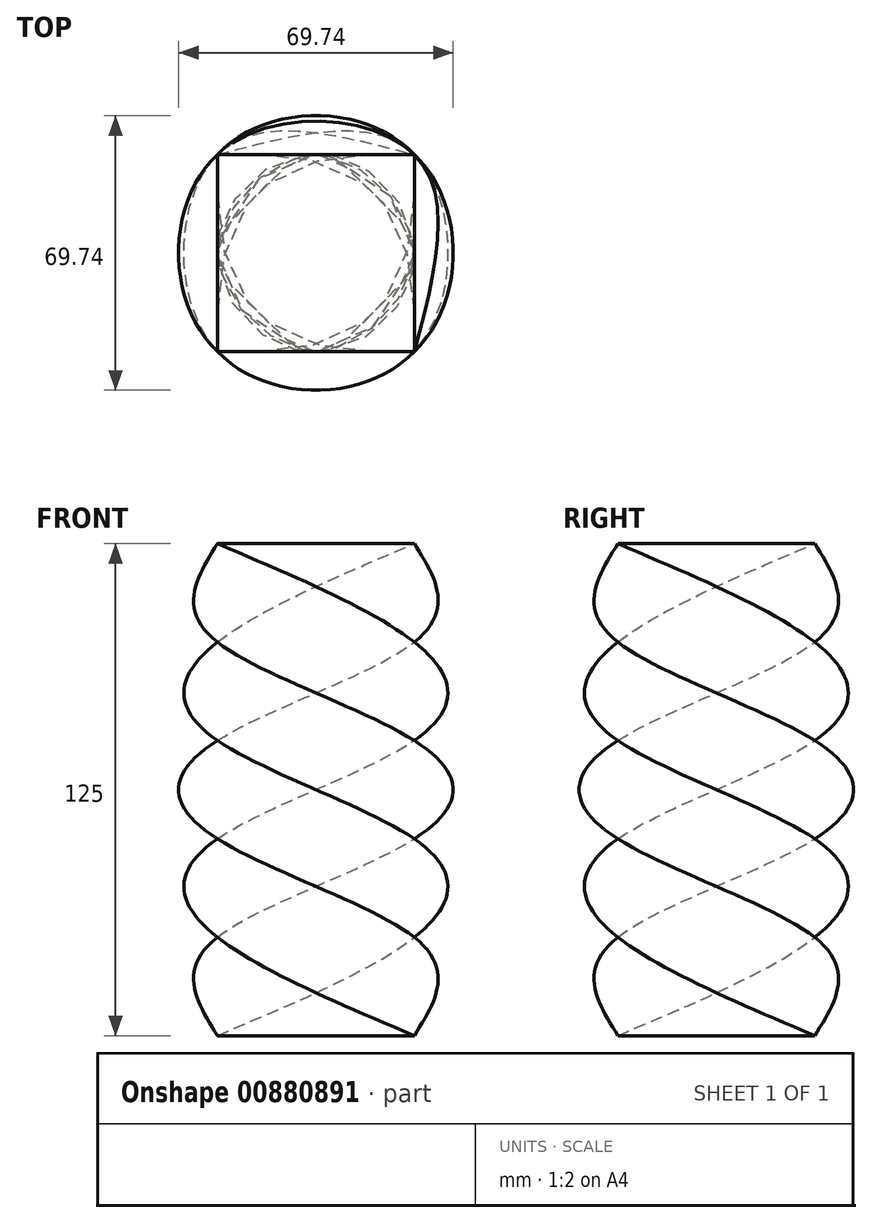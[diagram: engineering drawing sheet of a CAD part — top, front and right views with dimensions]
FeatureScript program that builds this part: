
annotation { "Feature Type Name" : "Feature", "Feature Type Description" : "" }
export const myFeature = defineFeature(function(context is Context, id is Id, definition is map)
    precondition{}
    {
        {
            var Q0;
            Q0=qCreatedBy(makeId("Top.planeOp"),FACE);
            cPlane(context, id + "F0", {"entities" : qUnion([Q0]), "cplaneType" : CPlaneType.OFFSET, "offset" : 25 * mm, "width" : 150 * mm, "height" : 150 * mm});
        }
        {
            var Q0;
            Q0=qCreatedBy(id+"F0.planeOp",FACE);
            cPlane(context, id + "F1", {"entities" : qUnion([Q0]), "cplaneType" : CPlaneType.OFFSET, "offset" : 25 * mm, "width" : 150 * mm, "height" : 150 * mm});
        }
        {
            var Q0;
            Q0=qCreatedBy(id+"F1.planeOp",FACE);
            cPlane(context, id + "F2", {"entities" : qUnion([Q0]), "cplaneType" : CPlaneType.OFFSET, "offset" : 25 * mm, "width" : 150 * mm, "height" : 150 * mm});
        }
        {
            var Q0;
            Q0=qCreatedBy(id+"F2.planeOp",FACE);
            cPlane(context, id + "F3", {"entities" : qUnion([Q0]), "cplaneType" : CPlaneType.OFFSET, "offset" : 25 * mm, "width" : 150 * mm, "height" : 150 * mm});
        }
        {
            var Q0;
            Q0=qCreatedBy(id+"F3.planeOp",FACE);
            cPlane(context, id + "F4", {"entities" : qUnion([Q0]), "cplaneType" : CPlaneType.OFFSET, "offset" : 25 * mm, "width" : 150 * mm, "height" : 150 * mm});
        }
        {
            var Q0;
            Q0=qCreatedBy(makeId("Top.planeOp"),FACE);
            var sketch = newSketch(context, id + "F5", { "sketchPlane" : qUnion([Q0])});
            skLineSegment(sketch, "E0.bottom", {"start": v(25, 25) * mm, "end": v(-25, 25) * mm});
            skLineSegment(sketch, "E0.top", {"start": v(25, -25) * mm, "end": v(-25, -25) * mm});
            skLineSegment(sketch, "E0.left", {"start": v(25, 25) * mm, "end": v(25, -25) * mm});
            skLineSegment(sketch, "E0.right", {"start": v(-25, 25) * mm, "end": v(-25, -25) * mm});
            skPoint(sketch, "E0.middle", {"position": v(0, 0) * mm});
            skSolve(sketch);
        }
        {
            var Q0;
            Q0=qCreatedBy(id+"F0.planeOp",FACE);
            var sketch = newSketch(context, id + "F6", { "sketchPlane" : qUnion([Q0])});
            skLineSegment(sketch, "E1.0", {"start": v(25, -25) * mm, "end": v(-25, -25) * mm});
            skLineSegment(sketch, "E2.0", {"start": v(25, 25) * mm, "end": v(25, -25) * mm});
            skLineSegment(sketch, "E3.0", {"start": v(-25, 25) * mm, "end": v(-25, -25) * mm});
            skLineSegment(sketch, "E4.0", {"start": v(25, 25) * mm, "end": v(-25, 25) * mm});
            skPoint(sketch, "E5.0", {"position": v(0, 0) * mm});
            skSolve(sketch);
        }
        {
            var Q0;
            Q0=qCreatedBy(id+"F1.planeOp",FACE);
            var sketch = newSketch(context, id + "F7", { "sketchPlane" : qUnion([Q0])});
            skPoint(sketch, "E6.0", {"position": v(0, 0) * mm});
            skLineSegment(sketch, "E7.0", {"start": v(-25, 25) * mm, "end": v(-25, -25) * mm});
            skLineSegment(sketch, "E8.0", {"start": v(25, 25) * mm, "end": v(25, -25) * mm});
            skLineSegment(sketch, "E9.0", {"start": v(25, -25) * mm, "end": v(-25, -25) * mm});
            skLineSegment(sketch, "E10.0", {"start": v(25, 25) * mm, "end": v(-25, 25) * mm});
            skSolve(sketch);
        }
        {
            var Q0;
            Q0=qCreatedBy(id+"F2.planeOp",FACE);
            var sketch = newSketch(context, id + "F8", { "sketchPlane" : qUnion([Q0])});
            skLineSegment(sketch, "E11.0", {"start": v(25, 25) * mm, "end": v(-25, 25) * mm});
            skLineSegment(sketch, "E12.0", {"start": v(-25, 25) * mm, "end": v(-25, -25) * mm});
            skLineSegment(sketch, "E13.0", {"start": v(25, 25) * mm, "end": v(25, -25) * mm});
            skPoint(sketch, "E14.0", {"position": v(0, 0) * mm});
            skLineSegment(sketch, "E15.0", {"start": v(25, -25) * mm, "end": v(-25, -25) * mm});
            skSolve(sketch);
        }
        {
            var Q0;
            Q0=qCreatedBy(id+"F3.planeOp",FACE);
            var sketch = newSketch(context, id + "F9", { "sketchPlane" : qUnion([Q0])});
            skLineSegment(sketch, "E16.0", {"start": v(25, 25) * mm, "end": v(-25, 25) * mm});
            skLineSegment(sketch, "E17.0", {"start": v(-25, 25) * mm, "end": v(-25, -25) * mm});
            skLineSegment(sketch, "E18.0", {"start": v(25, 25) * mm, "end": v(25, -25) * mm});
            skLineSegment(sketch, "E19.0", {"start": v(25, -25) * mm, "end": v(-25, -25) * mm});
            skPoint(sketch, "E20.0", {"position": v(0, 0) * mm});
            skSolve(sketch);
        }
        {
            var Q0;
            Q0=qCreatedBy(id+"F4.planeOp",FACE);
            var sketch = newSketch(context, id + "F10", { "sketchPlane" : qUnion([Q0])});
            skLineSegment(sketch, "E21.0", {"start": v(25, 25) * mm, "end": v(-25, 25) * mm});
            skLineSegment(sketch, "E22.0", {"start": v(25, 25) * mm, "end": v(25, -25) * mm});
            skLineSegment(sketch, "E23.0", {"start": v(-25, 25) * mm, "end": v(-25, -25) * mm});
            skLineSegment(sketch, "E24.0", {"start": v(25, -25) * mm, "end": v(-25, -25) * mm});
            skPoint(sketch, "E25.0", {"position": v(0, 0) * mm});
            skSolve(sketch);
        }
        {
            var Q0;
            Q0=makeQuery(id+"F5.imprint","IMPRINT",FACE,{"disambiguationData":[TD([[makeQuery(id+"F5.imprint","IMPRINT",EDGE,{"derivedFrom":sQuery(id+"F5.wireOp",EDGE,"E0.bottom")}),1.0]])]});
            var Q1;
            Q1=makeQuery(id+"F6.imprint","IMPRINT",FACE,{"disambiguationData":[TD([[makeQuery(id+"F6.imprint","IMPRINT",EDGE,{"derivedFrom":sQuery(id+"F6.wireOp",EDGE,"E1.0")}),-1.0]])]});
            var Q2;
            Q2=makeQuery(id+"F7.imprint","IMPRINT",FACE,{"disambiguationData":[TD([[makeQuery(id+"F7.imprint","IMPRINT",EDGE,{"derivedFrom":sQuery(id+"F7.wireOp",EDGE,"E7.0")}),1.0]])]});
            var Q3;
            Q3=makeQuery(id+"F8.imprint","IMPRINT",FACE,{"disambiguationData":[TD([[makeQuery(id+"F8.imprint","IMPRINT",EDGE,{"derivedFrom":sQuery(id+"F8.wireOp",EDGE,"E11.0")}),1.0]])]});
            var Q4;
            Q4=makeQuery(id+"F9.imprint","IMPRINT",FACE,{"disambiguationData":[TD([[makeQuery(id+"F9.imprint","IMPRINT",EDGE,{"derivedFrom":sQuery(id+"F9.wireOp",EDGE,"E16.0")}),1.0]])]});
            var Q5;
            Q5=makeQuery(id+"F10.imprint","IMPRINT",FACE,{"disambiguationData":[TD([[makeQuery(id+"F10.imprint","IMPRINT",EDGE,{"derivedFrom":sQuery(id+"F10.wireOp",EDGE,"E21.0")}),1.0]])]});
            var Q6;
            Q6=sQuery(id+"F5.wireOp",VERTEX,"E0.top.end");
            var Q7;
            Q7=sQuery(id+"F6.wireOp",VERTEX,"E3.0.start");
            var Q8;
            Q8=sQuery(id+"F7.wireOp",VERTEX,"E8.0.start");
            var Q9;
            Q9=sQuery(id+"F8.wireOp",VERTEX,"E13.0.end");
            var Q10;
            Q10=sQuery(id+"F9.wireOp",VERTEX,"E17.0.end");
            var Q11;
            Q11=sQuery(id+"F10.wireOp",VERTEX,"E21.0.end");
            loft(context, id + "F11", {"sheetProfilesArray" : [{ "sheetProfileEntities" : qUnion([Q0]) }, { "sheetProfileEntities" : qUnion([Q1]) }, { "sheetProfileEntities" : qUnion([Q2]) }, { "sheetProfileEntities" : qUnion([Q3]) }, { "sheetProfileEntities" : qUnion([Q4]) }, { "sheetProfileEntities" : qUnion([Q5]) }], "matchConnections" : true, "connections" : [{ "connectionEntities" : qUnion([Q6, Q7, Q8, Q9, Q10, Q11]), "connectionEdgeQueries" : qUnion([]), "connectionEdgeParameters" : [] }]});
        }
    });
